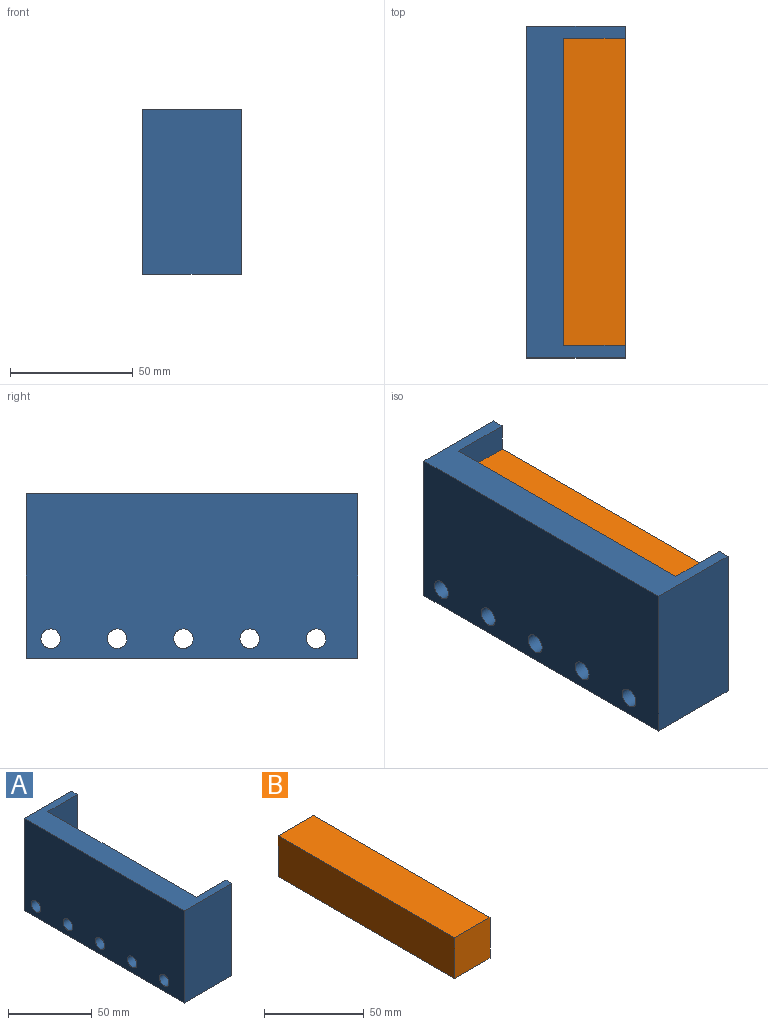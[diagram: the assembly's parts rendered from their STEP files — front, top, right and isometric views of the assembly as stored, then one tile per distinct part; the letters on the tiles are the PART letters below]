
ASSEMBLY  parts=2 mates=1
PART A: 22 faces, bbox 40x135x67.1 mm
  f0: plane 135x67.1mm, normal (1,0,0), area 3516.4mm2, adj f1,f2,f3,f5,f7,f8,f9,f10
  f1: plane 125x25mm, normal (0,0,1), area 3125mm2, adj f0,f3,f4,f21
  f2: plane 135x40mm, normal (0,0,-1), area 5400mm2, adj f0,f5,f6,f20
  f3: plane 42.1x25mm, normal (0,-1,0), area 1052.5mm2, adj f0,f1,f4,f7
  f4: plane 125x42.1mm, normal (1,0,0), area 5262.5mm2, adj f1,f3,f7,f21
  f5: plane 67.1x40mm, normal (0,1,0), area 2598.4mm2, adj f0,f2,f6,f7,f13,f14,f15,f18
  f6: plane 135x67.1mm, normal (-1,0,0), area 8807.2mm2, adj f2,f5,f7,f8,f9,f10,f11,f12
  f7: plane 135x40mm, normal (0,0,1), area 2275mm2, adj f0,f3,f4,f5,f6,f20,f21
  f8: cylinder r=4mm len=40mm, axis (-1,0,0), area 1005.3mm2, adj f0,f6
  f9: cylinder r=4mm len=40mm, axis (-1,0,0), area 1005.3mm2, adj f0,f6
  f10: cylinder r=4mm len=40mm, axis (-1,0,0), area 1005.3mm2, adj f0,f6
  f11: cylinder r=4mm len=40mm, axis (-1,0,0), area 1005.3mm2, adj f0,f6
  f12: cylinder r=4mm len=40mm, axis (-1,0,0), area 1005.3mm2, adj f0,f6
  f13: cylinder r=3mm len=124mm, axis (0,1,0), area 2301.3mm2, adj f5,f16
  f14: cylinder r=3mm len=124mm, axis (0,1,0), area 2301.3mm2, adj f5,f16
  f15: cylinder r=3mm len=124mm, axis (0,1,0), area 2301.3mm2, adj f5,f16
  f16: cylinder r=3mm len=30mm, axis (1,0,0), area 457.5mm2, adj f0,f13,f14,f15,f17
  f17: plane 6x6mm, normal (1,0,0), area 28.3mm2, adj f16
  f18: cylinder r=0.5mm len=67.5mm, axis (0,1,0), area 212.1mm2, adj f5,f19
  f19: plane 1x1mm, normal (0,1,0), area 0.8mm2, adj f18
  f20: plane 67.1x40mm, normal (0,-1,0), area 2684mm2, adj f0,f2,f6,f7
  f21: plane 42.1x25mm, normal (0,1,0), area 1052.5mm2, adj f0,f1,f4,f7
PART B: 6 faces, bbox 25x125x25 mm
  f0: plane 25x25mm, normal (0,1,0), area 625mm2, adj f1,f3,f4,f5
  f1: plane 125x25mm, normal (-1,0,0), area 3125mm2, adj f0,f2,f4,f5
  f2: plane 25x25mm, normal (0,-1,0), area 625mm2, adj f1,f3,f4,f5
  f3: plane 125x25mm, normal (1,0,0), area 3125mm2, adj f0,f2,f4,f5
  f4: plane 125x25mm, normal (0,0,1), area 3125mm2, adj f0,f1,f2,f3
  f5: plane 125x25mm, normal (0,0,-1), area 3125mm2, adj f0,f1,f2,f3
PLACE A t=(-5,62.5,0)mm
PLACE B rot(axis=(0,1,0),180deg) t=(20,62.5,55.64)mm
MATE slider A.f1 <-> B.f4  axis (0,0,1) through (7.5,0,25)mm
